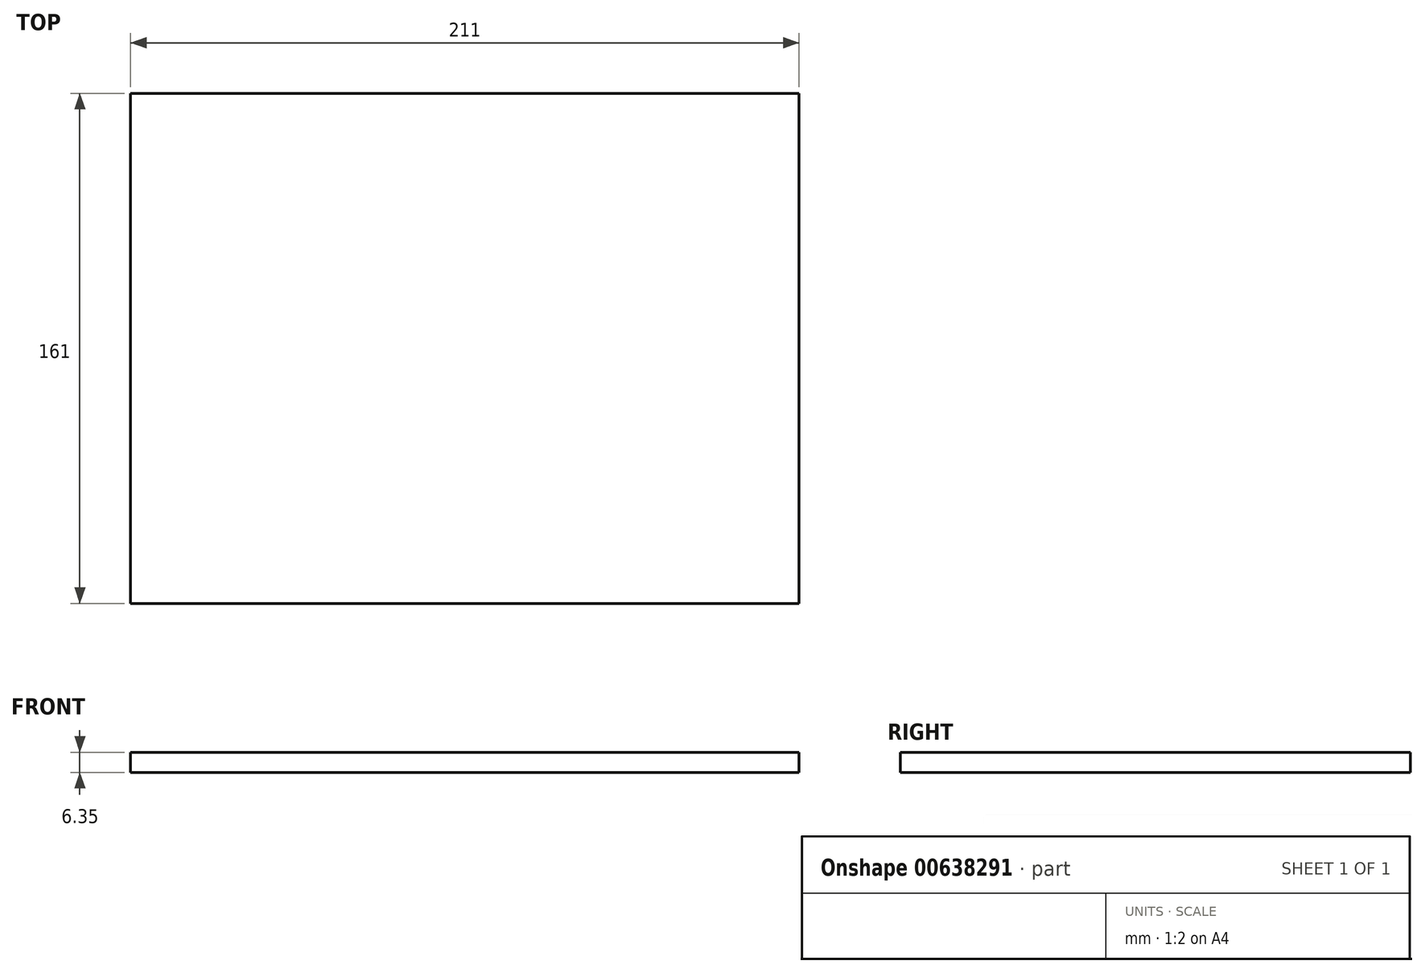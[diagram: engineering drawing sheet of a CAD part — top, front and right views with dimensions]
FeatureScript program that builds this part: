
annotation { "Feature Type Name" : "Feature", "Feature Type Description" : "" }
export const myFeature = defineFeature(function(context is Context, id is Id, definition is map)
    precondition{}
    {
        {
            var Q0;
            Q0=qCreatedBy(makeId("Top.planeOp"),FACE);
            var sketch = newSketch(context, id + "F0", { "sketchPlane" : qUnion([Q0])});
            skLineSegment(sketch, "E0.bottom", {"start": v(0, 0) * mm, "end": v(211, 0) * mm});
            skLineSegment(sketch, "E0.top", {"start": v(0, -161) * mm, "end": v(211, -161) * mm});
            skLineSegment(sketch, "E0.left", {"start": v(0, 0) * mm, "end": v(0, -161) * mm});
            skLineSegment(sketch, "E0.right", {"start": v(211, 0) * mm, "end": v(211, -161) * mm});
            skSolve(sketch);
        }
        {
            var Q0;
            Q0=makeQuery(id+"F0.imprint","IMPRINT",FACE,{"disambiguationData":[TD([[makeQuery(id+"F0.imprint","IMPRINT",EDGE,{"derivedFrom":sQuery(id+"F0.wireOp",EDGE,"E0.bottom")}),-1.0]])]});
            extrude(context, id + "F1", {"entities" : qUnion([Q0]), "depth" : 6.35 * mm, "offsetDistance" : 25.4 * mm});
        }
    });
